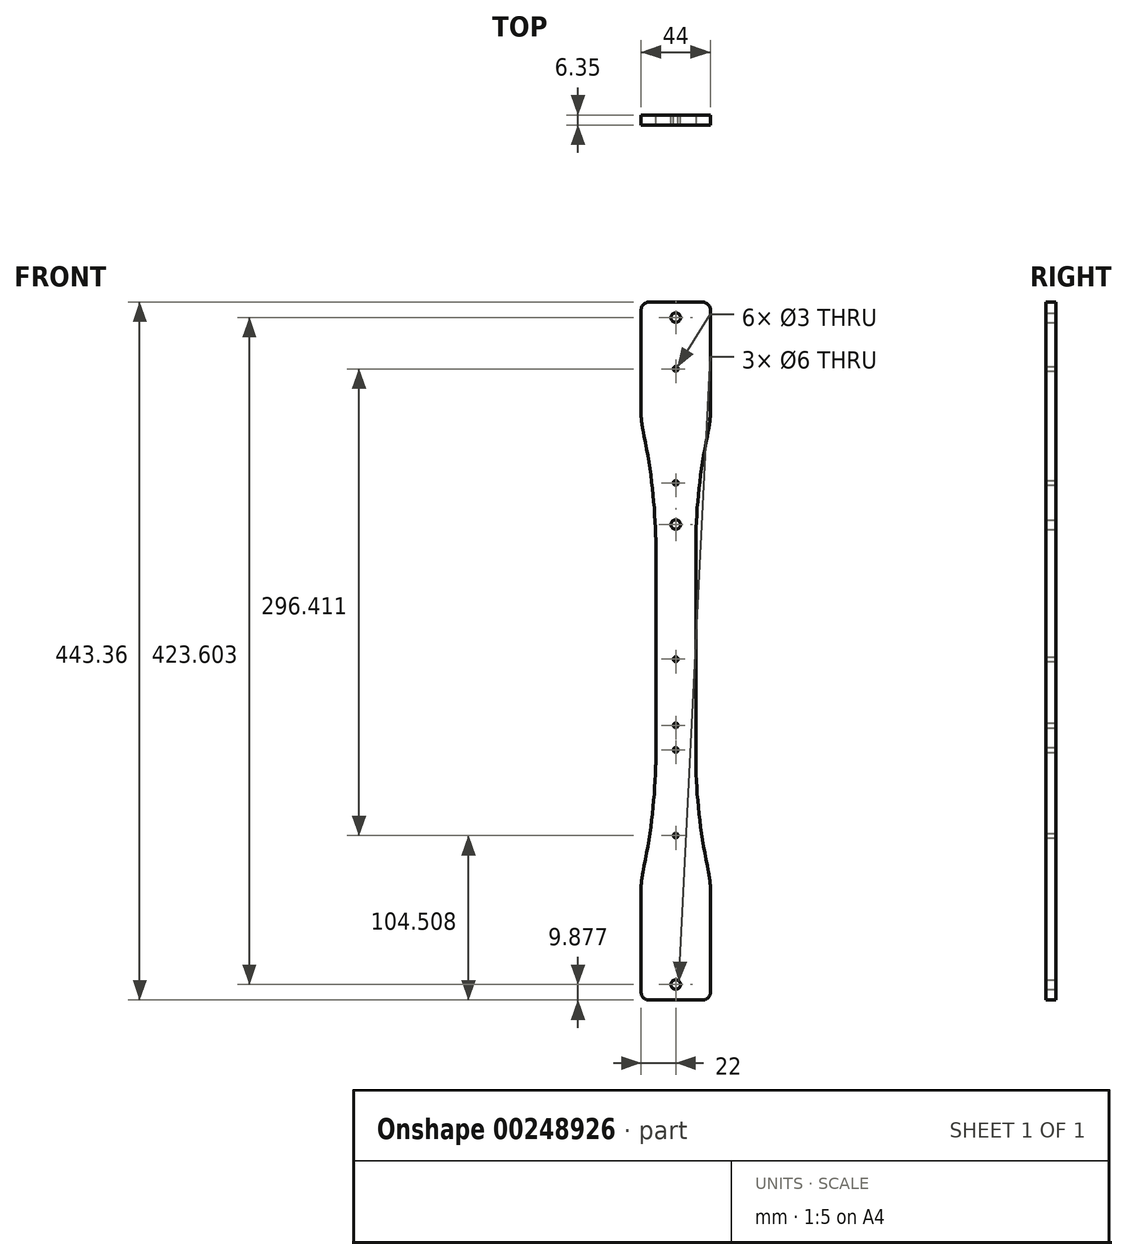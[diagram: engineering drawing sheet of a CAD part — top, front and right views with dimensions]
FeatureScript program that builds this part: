
annotation { "Feature Type Name" : "Feature", "Feature Type Description" : "" }
export const myFeature = defineFeature(function(context is Context, id is Id, definition is map)
    precondition{}
    {
        {
            var Q0;
            Q0=qCreatedBy(makeId("Front.planeOp"),FACE);
            var sketch = newSketch(context, id + "F0", { "sketchPlane" : qUnion([Q0])});
            skCircle(sketch, "E0", {"center": v(0, -85.45) * mm, "radius": 1.5 * mm});
            skCircle(sketch, "E1", {"center": v(0, -31.07) * mm, "radius": 1.5 * mm});
            skCircle(sketch, "E2", {"center": v(0, 26.55) * mm, "radius": 1.5 * mm});
            skLineSegment(sketch, "E3.top", {"start": v(-4.69, -189.96) * mm, "end": v(4.69, -189.96) * mm});
            skPoint(sketch, "E4.visualSharp", {"position": v(12.7, -189.96) * mm});
            skPoint(sketch, "E5.visualSharp", {"position": v(-12.7, -189.96) * mm});
            skLineSegment(sketch, "E6", {"start": v(0, 26.55) * mm, "end": v(0, 99.81) * mm, "construction": true});
            skLineSegment(sketch, "E7", {"start": v(0, 99.81) * mm, "end": v(0, -85.45) * mm, "construction": true});
            skLineSegment(sketch, "E8", {"start": v(0, -85.45) * mm, "end": v(0, -201.73) * mm, "construction": true});
            skCircle(sketch, "E9", {"center": v(0, 243.52) * mm, "radius": 3 * mm});
            skCircle(sketch, "E10", {"center": v(0, -15.48) * mm, "radius": 1.5 * mm});
            skLineSegment(sketch, "E11", {"start": v(0, 58.56) * mm, "end": v(0, 424.12) * mm});
            skCircle(sketch, "E12", {"center": v(0, 210.96) * mm, "radius": 1.5 * mm});
            skCircle(sketch, "E13", {"center": v(0, 138.56) * mm, "radius": 1.5 * mm});
            skLineSegment(sketch, "E14", {"start": v(12.7, 31.72) * mm, "end": v(-12.7, 31.72) * mm, "construction": true});
            skLineSegment(sketch, "E15.MirrorCS", {"start": v(-4.69, 253.4) * mm, "end": v(4.69, 253.4) * mm});
            skPoint(sketch, "E16.orphan", {"position": v(-7.5, 253.51) * mm});
            skPoint(sketch, "E17.start.orphan", {"position": v(7.5, 253.51) * mm});
            skCircle(sketch, "E18", {"center": v(0, -180.08) * mm, "radius": 3 * mm});
            skCircle(sketch, "E19", {"center": v(0, 112.09) * mm, "radius": 3 * mm});
            skLineSegment(sketch, "E20.trimOffspring", {"start": v(-12.7, 104.8) * mm, "end": v(-12.7, -41.36) * mm});
            skLineSegment(sketch, "E21.trimOffspring", {"start": v(12.7, 104.8) * mm, "end": v(12.7, -41.36) * mm});
            skLineSegment(sketch, "E22", {"start": v(-22, 177.54) * mm, "end": v(-22, 236.3) * mm});
            skLineSegment(sketch, "E23.MirrorCS", {"start": v(22, 177.54) * mm, "end": v(22, 236.3) * mm});
            skArc(sketch, "E24", {"start": v(-12.7, 104.8) * mm, "mid": v(-15.58, 141.4) * mm, "end": v(-22, 177.54) * mm});
            skArc(sketch, "E25.MirrorCS", {"start": v(12.7, 104.8) * mm, "mid": v(15.58, 141.4) * mm, "end": v(22, 177.54) * mm});
            skPoint(sketch, "E26.orphan", {"position": v(-4.69, 253.4) * mm});
            skPoint(sketch, "E27.orphan", {"position": v(-22, 240.87) * mm});
            skPoint(sketch, "E28.orphan", {"position": v(4.69, 253.4) * mm});
            skPoint(sketch, "E29.orphan", {"position": v(22, 240.87) * mm});
            skLineSegment(sketch, "E30", {"start": v(0, 253.4) * mm, "end": v(-22, 253.4) * mm});
            skLineSegment(sketch, "E31", {"start": v(-22, 225.43) * mm, "end": v(-22, 253.4) * mm});
            skLineSegment(sketch, "E32.MirrorCS", {"start": v(22, 225.43) * mm, "end": v(22, 253.4) * mm});
            skLineSegment(sketch, "E33.MirrorCS", {"start": v(0, 253.4) * mm, "end": v(22, 253.4) * mm});
            skArc(sketch, "E34.MirrorCS", {"start": v(12.7, -41.36) * mm, "mid": v(15.58, -77.96) * mm, "end": v(22, -114.1) * mm});
            skLineSegment(sketch, "E35.MirrorCS", {"start": v(22, -114.1) * mm, "end": v(22, -172.87) * mm});
            skArc(sketch, "E36.MirrorCS", {"start": v(-12.7, -41.36) * mm, "mid": v(-15.58, -77.96) * mm, "end": v(-22, -114.1) * mm});
            skLineSegment(sketch, "E37.MirrorCS", {"start": v(-22, -114.1) * mm, "end": v(-22, -162) * mm});
            skLineSegment(sketch, "E38.MirrorCS", {"start": v(-4.69, -189.96) * mm, "end": v(-22, -189.96) * mm});
            skLineSegment(sketch, "E39.MirrorCS", {"start": v(4.69, -189.96) * mm, "end": v(22, -189.96) * mm});
            skLineSegment(sketch, "E40.MirrorCS", {"start": v(22, -172.87) * mm, "end": v(22, -189.96) * mm});
            skLineSegment(sketch, "E41.MirrorCS", {"start": v(-22, -162) * mm, "end": v(-22, -189.96) * mm});
            skPoint(sketch, "E42.orphan", {"position": v(-22, -172.87) * mm});
            skPoint(sketch, "E43.orphan", {"position": v(22, -162) * mm});
            skPoint(sketch, "E44.orphan", {"position": v(0, -189.96) * mm});
            skSolve(sketch);
        }
        {
            var Q0;
            Q0=makeQuery(id+"F0.imprint","IMPRINT",FACE,{"disambiguationData":[TD([[makeQuery(id+"F0.imprint","IMPRINT",EDGE,{"derivedFrom":sQuery(id+"F0.wireOp",EDGE,"E0")}),-1.0]])]});
            var Q1;
            {var subQ8=sQuery(id+"F0.wireOp",EDGE,"E3.left");Q1=makeQuery(id+"F0.imprint","IMPRINT",FACE,{"disambiguationData":[TD([[makeQuery(id+"F0.imprint","IMPRINT",EDGE,{"derivedFrom":subQ8}),-1.0]])]});}
            var Q2;
            {var subQ10=sQuery(id+"F0.wireOp",EDGE,"E3.right");Q2=makeQuery(id+"F0.imprint","IMPRINT",FACE,{"disambiguationData":[TD([[makeQuery(id+"F0.imprint","IMPRINT",EDGE,{"derivedFrom":subQ10}),1.0]])]});}
            var Q3;
            {var subQ8=sQuery(id+"F0.wireOp",EDGE,"E3.right");Q3=makeQuery(id+"F0.imprint","IMPRINT",FACE,{"disambiguationData":[TD([[makeQuery(id+"F0.imprint","IMPRINT",EDGE,{"derivedFrom":subQ8}),-1.0]])]});}
            var Q4;
            {var subQ8=sQuery(id+"F0.wireOp",EDGE,"E3.left");Q4=makeQuery(id+"F0.imprint","IMPRINT",FACE,{"disambiguationData":[TD([[makeQuery(id+"F0.imprint","IMPRINT",EDGE,{"derivedFrom":subQ8}),1.0]])]});}
            var Q5;
            {var subQ0=sQuery(id+"F0.wireOp",EDGE,"ywFLEBLb-G5Qe-hJVo-9jNG-EmXgII5EXrAz");Q5=makeQuery(id+"F0.imprint","IMPRINT",FACE,{"disambiguationData":[TD([[makeQuery(id+"F0.imprint","IMPRINT",EDGE,{"derivedFrom":subQ0}),-1.0]])]});}
            var Q6;
            {var subQ17=sQuery(id+"F0.wireOp",EDGE,"E22");Q6=makeQuery(id+"F0.imprint","IMPRINT",FACE,{"disambiguationData":[TD([[makeQuery(id+"F0.imprint","IMPRINT",EDGE,{"derivedFrom":subQ17}),-1.0]])]});}
            var Q7;
            {var subQ4=sQuery(id+"F0.wireOp",EDGE,"E23.MirrorCS");Q7=makeQuery(id+"F0.imprint","IMPRINT",FACE,{"disambiguationData":[TD([[makeQuery(id+"F0.imprint","IMPRINT",EDGE,{"derivedFrom":subQ4}),1.0]])]});}
            var Q8;
            {var subQ2=sQuery(id+"F0.wireOp",EDGE,"E4.filletArc");Q8=makeQuery(id+"F0.imprint","IMPRINT",FACE,{"disambiguationData":[TD([[makeQuery(id+"F0.imprint","IMPRINT",EDGE,{"derivedFrom":subQ2}),-1.0]])]});}
            var Q9;
            {var subQ1=sQuery(id+"F0.wireOp",EDGE,"E4.filletArc");Q9=makeQuery(id+"F0.imprint","IMPRINT",FACE,{"disambiguationData":[TD([[makeQuery(id+"F0.imprint","IMPRINT",EDGE,{"derivedFrom":subQ1}),1.0]])]});}
            extrude(context, id + "F1", {"entities" : qUnion([Q0, Q1, Q2, Q3, Q4, Q5, Q6, Q7, Q8, Q9]), "depth" : 6.35 * mm});
        }
        {
            var Q0;
            Q0=makeQuery(id+"F1.opExtrude","SWEPT_EDGE",EDGE,{"disambiguationData":[OSD([sQuery(id+"F0.wireOp",EDGE,"E30"),sQuery(id+"F0.wireOp",EDGE,"E31")])]});
            var Q1;
            Q1=makeQuery(id+"F1.opExtrude","SWEPT_EDGE",EDGE,{"disambiguationData":[OSD([sQuery(id+"F0.wireOp",EDGE,"E32.MirrorCS"),sQuery(id+"F0.wireOp",EDGE,"E33.MirrorCS")])]});
            var Q2;
            Q2=makeQuery(id+"F1.opExtrude","SWEPT_EDGE",EDGE,{"disambiguationData":[OSD([sQuery(id+"F0.wireOp",EDGE,"E39.MirrorCS"),sQuery(id+"F0.wireOp",EDGE,"E40.MirrorCS")])]});
            var Q3;
            Q3=makeQuery(id+"F1.opExtrude","SWEPT_EDGE",EDGE,{"disambiguationData":[OSD([sQuery(id+"F0.wireOp",EDGE,"E38.MirrorCS"),sQuery(id+"F0.wireOp",EDGE,"E41.MirrorCS")])]});
            fillet(context, id + "F2", {"entities" : qUnion([Q0, Q1, Q2, Q3]), "radius" : 5.08 * mm, "tangentPropagation" : true, "allowEdgeOverflow" : false});
        }
        {
            var Q0;
            Q0=makeQuery(id+"F1.opExtrude","SWEPT_EDGE",EDGE,{"disambiguationData":[OSD([sQuery(id+"F0.wireOp",EDGE,"E36.MirrorCS"),sQuery(id+"F0.wireOp",EDGE,"E37.MirrorCS")])]});
            var Q1;
            Q1=makeQuery(id+"F1.opExtrude","SWEPT_EDGE",EDGE,{"disambiguationData":[OSD([sQuery(id+"F0.wireOp",EDGE,"E34.MirrorCS"),sQuery(id+"F0.wireOp",EDGE,"E35.MirrorCS")])]});
            var Q2;
            Q2=makeQuery(id+"F1.opExtrude","SWEPT_EDGE",EDGE,{"disambiguationData":[OSD([sQuery(id+"F0.wireOp",EDGE,"E23.MirrorCS"),sQuery(id+"F0.wireOp",EDGE,"E25.MirrorCS")])]});
            var Q3;
            Q3=makeQuery(id+"F1.opExtrude","SWEPT_EDGE",EDGE,{"disambiguationData":[OSD([sQuery(id+"F0.wireOp",EDGE,"E22"),sQuery(id+"F0.wireOp",EDGE,"E24")])]});
            var Q4;
            Q4=makeQuery(id+"F1.opExtrude","SWEPT_EDGE",EDGE,{"disambiguationData":[OSD([sQuery(id+"F0.wireOp",EDGE,"E20.trimOffspring"),sQuery(id+"F0.wireOp",EDGE,"E24")])]});
            var Q5;
            Q5=makeQuery(id+"F1.opExtrude","SWEPT_EDGE",EDGE,{"disambiguationData":[OSD([sQuery(id+"F0.wireOp",EDGE,"E21.trimOffspring"),sQuery(id+"F0.wireOp",EDGE,"E25.MirrorCS")])]});
            var Q6;
            Q6=makeQuery(id+"F1.opExtrude","SWEPT_EDGE",EDGE,{"disambiguationData":[OSD([sQuery(id+"F0.wireOp",EDGE,"E21.trimOffspring"),sQuery(id+"F0.wireOp",EDGE,"E34.MirrorCS")])]});
            var Q7;
            Q7=makeQuery(id+"F1.opExtrude","SWEPT_EDGE",EDGE,{"disambiguationData":[OSD([sQuery(id+"F0.wireOp",EDGE,"E20.trimOffspring"),sQuery(id+"F0.wireOp",EDGE,"E36.MirrorCS")])]});
            fillet(context, id + "F3", {"entities" : qUnion([Q0, Q1, Q2, Q3, Q4, Q5, Q6, Q7]), "radius" : 50.8 * mm, "tangentPropagation" : true, "allowEdgeOverflow" : false});
        }
    });
